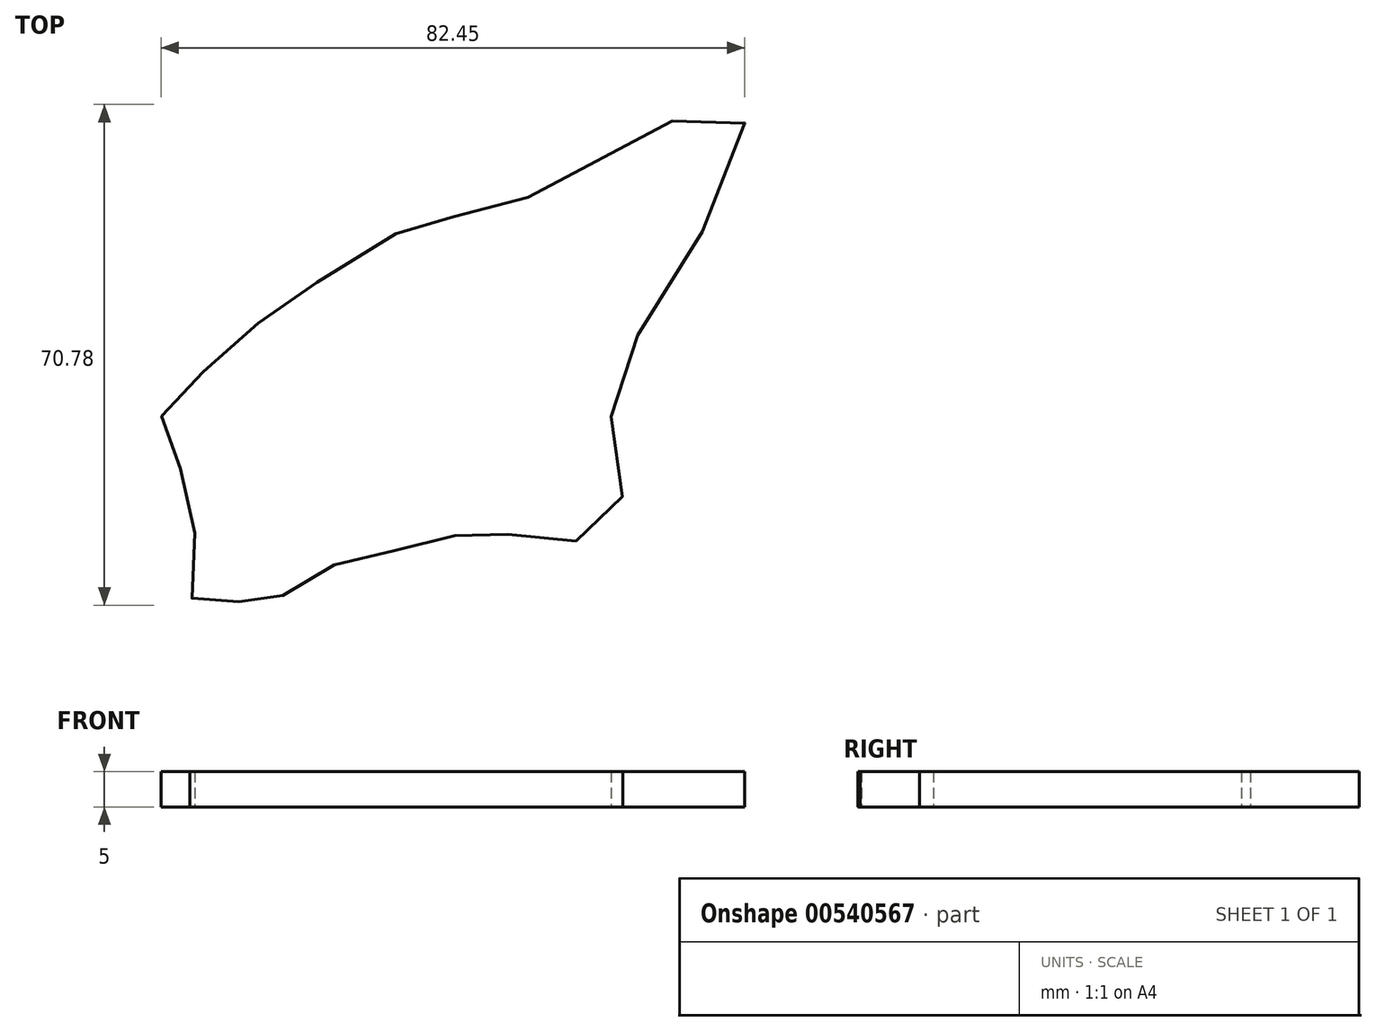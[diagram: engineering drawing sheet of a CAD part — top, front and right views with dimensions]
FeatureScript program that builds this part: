
annotation { "Feature Type Name" : "Feature", "Feature Type Description" : "" }
export const myFeature = defineFeature(function(context is Context, id is Id, definition is map)
    precondition{}
    {
        {
            var Q0;
            Q0=qCreatedBy(makeId("Top.planeOp"),FACE);
            var sketch = newSketch(context, id + "F0", { "sketchPlane" : qUnion([Q0])});
            skFitSpline(sketch, "E0", {"points": [v(-71, 18.83) * mm, v(-73.74, 25.89) * mm, v(-68.25, 32.16) * mm, v(-58.84, 40.4) * mm, v(-47.46, 47.85) * mm, v(-33.34, 54.91) * mm, v(-30.2, 53.74) * mm, v(7.06, 70.21) * mm, v(0, 47.85) * mm, v(-10.2, 27.06) * mm, v(-9.02, 12.94) * mm, v(-18.83, 8.24) * mm, v(-27.85, 10.2) * mm, v(-34.52, 8.63) * mm, v(-43.93, 6.67) * mm, v(-52.17, 3.92) * mm, v(-58.44, 0) * mm, v(-63.15, 0) * mm, v(-69.03, 0) * mm, v(-69.03, 8.63) * mm, v(-71, 18.83) * mm]});
            skSolve(sketch);
        }
        {
            var Q0;
            Q0=makeQuery(id+"F0.imprint","IMPRINT",FACE,{"disambiguationData":[TD([[makeQuery(id+"F0.imprint","IMPRINT",EDGE,{"derivedFrom":sQuery(id+"F0.wireOp",EDGE,"E0")}),-1.0]])]});
            extrude(context, id + "F1", {"entities" : qUnion([Q0]), "depth" : 5 * mm, "offsetDistance" : 25 * mm});
        }
    });
